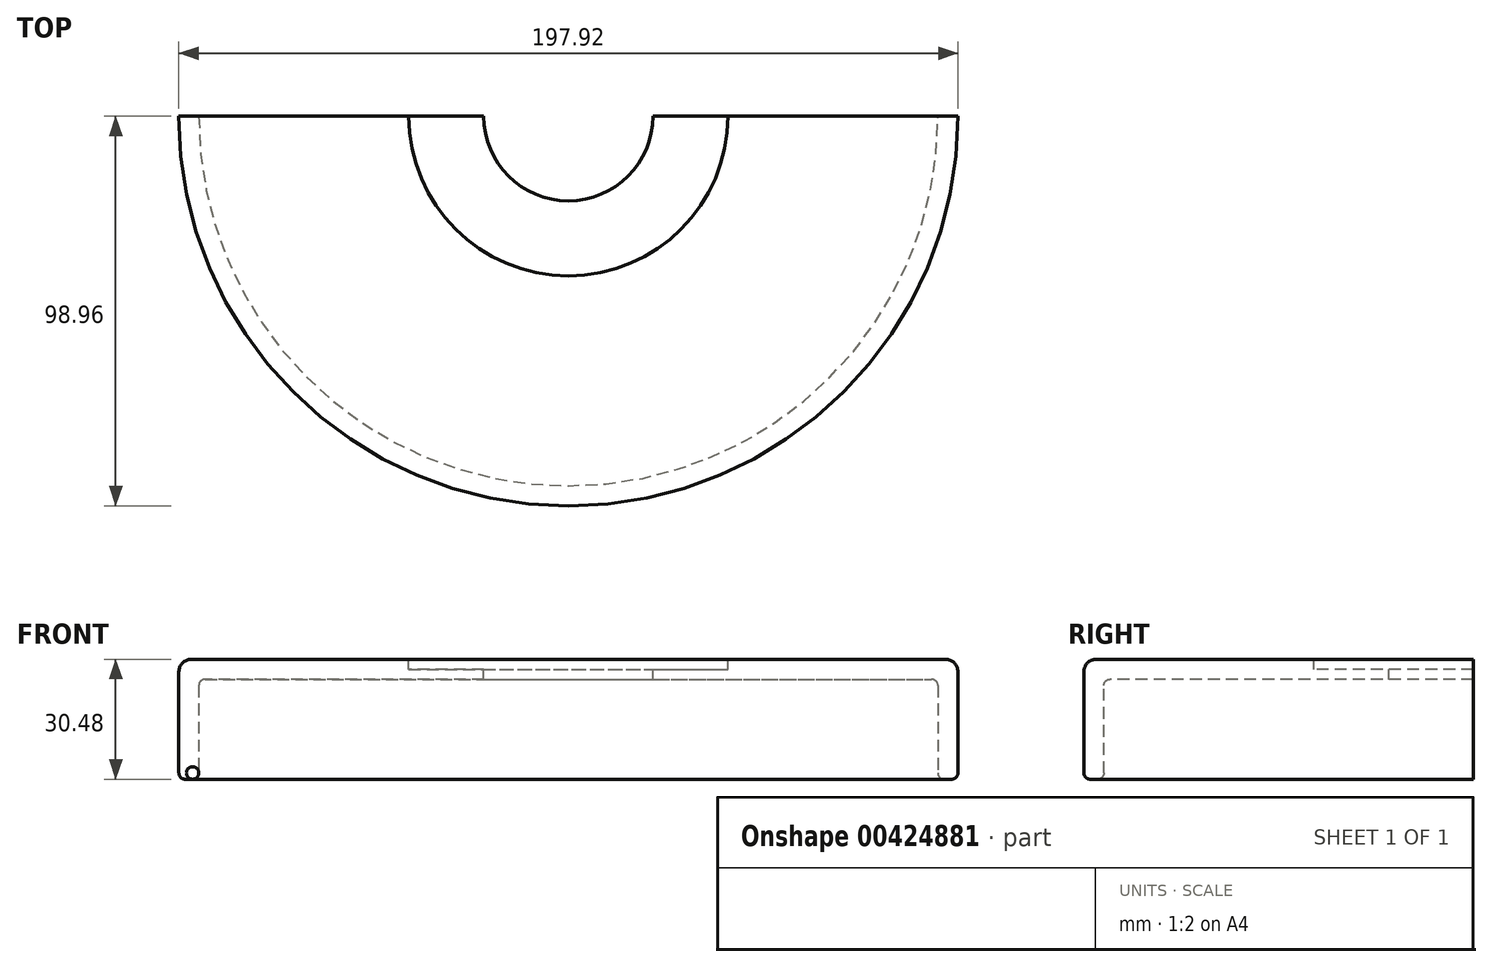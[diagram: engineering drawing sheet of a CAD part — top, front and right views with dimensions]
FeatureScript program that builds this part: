
annotation { "Feature Type Name" : "Feature", "Feature Type Description" : "" }
export const myFeature = defineFeature(function(context is Context, id is Id, definition is map)
    precondition{}
    {
        {
            var Q0;
            Q0=qCreatedBy(makeId("Front.planeOp"),FACE);
            var sketch = newSketch(context, id + "F0", { "sketchPlane" : qUnion([Q0])});
            skLineSegment(sketch, "E0", {"start": v(95.78, 5.08) * mm, "end": v(40.54, 5.08) * mm});
            skLineSegment(sketch, "E1", {"start": v(0, 102.6) * mm, "end": v(0, -103.27) * mm, "construction": true});
            skLineSegment(sketch, "E2", {"start": v(21.49, 0) * mm, "end": v(92.3, 0) * mm});
            skLineSegment(sketch, "E3", {"start": v(21.49, 0) * mm, "end": v(21.49, 2.54) * mm});
            skLineSegment(sketch, "E4", {"start": v(21.49, 2.54) * mm, "end": v(40.54, 2.54) * mm});
            skLineSegment(sketch, "E5", {"start": v(40.54, 2.54) * mm, "end": v(40.54, 5.08) * mm});
            skLineSegment(sketch, "E6", {"start": v(93.88, -1.59) * mm, "end": v(93.88, -23.81) * mm});
            skLineSegment(sketch, "E7", {"start": v(98.96, 1.9) * mm, "end": v(98.96, -23.81) * mm});
            skLineSegment(sketch, "E8", {"start": v(95.47, -25.4) * mm, "end": v(97.37, -25.4) * mm});
            skPoint(sketch, "E9.visualSharp", {"position": v(98.96, 5.08) * mm});
            skArc(sketch, "E9.filletArc", {"start": v(98.96, 1.9) * mm, "mid": v(98.03, 4.15) * mm, "end": v(95.78, 5.08) * mm});
            skPoint(sketch, "E10.visualSharp", {"position": v(93.88, -25.4) * mm});
            skArc(sketch, "E10.filletArc", {"start": v(93.88, -23.81) * mm, "mid": v(94.34, -24.94) * mm, "end": v(95.47, -25.4) * mm});
            skPoint(sketch, "E11.visualSharp", {"position": v(98.96, -25.4) * mm});
            skArc(sketch, "E11.filletArc", {"start": v(97.37, -25.4) * mm, "mid": v(98.5, -24.94) * mm, "end": v(98.96, -23.81) * mm});
            skPoint(sketch, "E12.visualSharp", {"position": v(93.88, 0) * mm});
            skArc(sketch, "E12.filletArc", {"start": v(93.88, -1.59) * mm, "mid": v(93.41, -0.46) * mm, "end": v(92.3, 0) * mm});
            skSolve(sketch);
        }
        {
            var Q0;
            Q0=makeQuery(id+"F0.imprint","IMPRINT",FACE,{"disambiguationData":[TD([[makeQuery(id+"F0.imprint","IMPRINT",EDGE,{"derivedFrom":sQuery(id+"F0.wireOp",EDGE,"E0")}),1.0]])]});
            var Q1;
            Q1=sQuery(id+"F0.wireOp",EDGE,"E1");
            revolve(context, id + "F1", {"entities" : qUnion([Q0]), "axis" : qUnion([Q1]), "revolveType" : RevolveType.ONE_DIRECTION, "angle" : 180 * degree});
        }
    });
